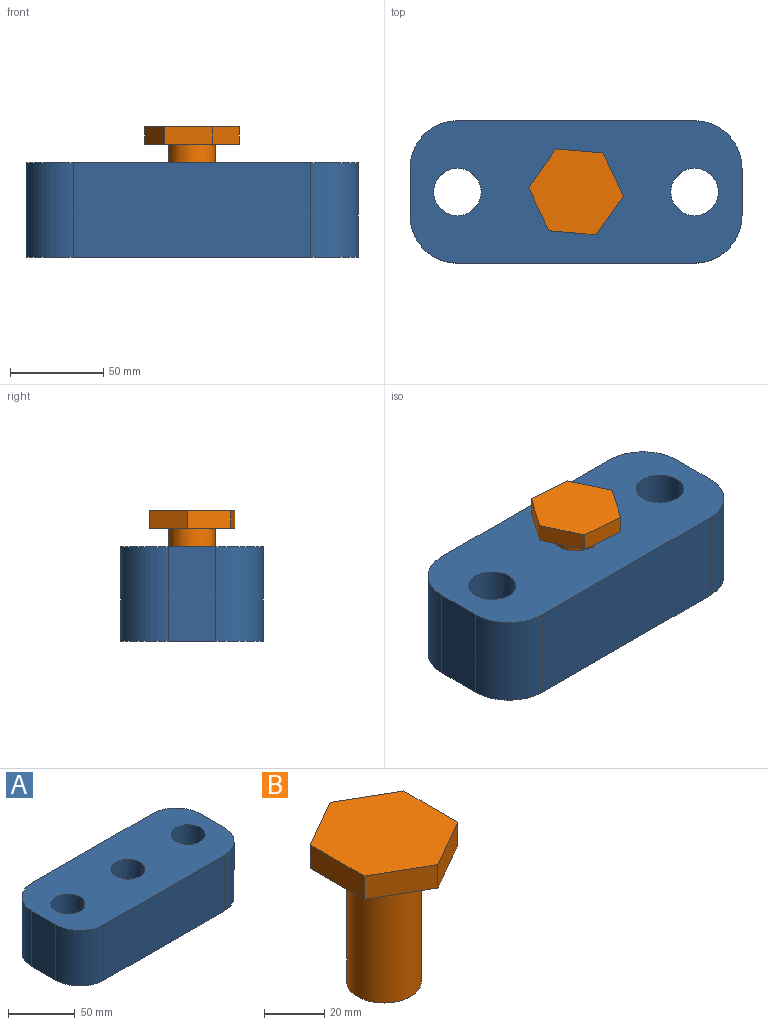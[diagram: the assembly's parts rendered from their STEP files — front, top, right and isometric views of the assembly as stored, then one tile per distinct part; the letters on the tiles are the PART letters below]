
ASSEMBLY  parts=2 mates=1
PART A: 13 faces, bbox 177.8x76.2x50.8 mm
  f0: plane 127x50.8mm, normal (0,1,0), area 6451.6mm2, adj f2,f3,f9,f12
  f1: plane 127x50.8mm, normal (0,-1,0), area 6451.6mm2, adj f2,f3,f10,f11
  f2: plane 177.8x76.2mm, normal (0,0,1), area 11474.4mm2, adj f0,f1,f4,f5,f6,f7,f8,f9
  f3: plane 177.8x76.2mm, normal (0,0,-1), area 11474.4mm2, adj f0,f1,f4,f5,f6,f7,f8,f9
  f4: cylinder r=12.7mm len=50.8mm, axis (0,0,1), area 4053.7mm2, adj f2,f3
  f5: plane 50.8x25.4mm, normal (-1,0,0), area 1290.3mm2, adj f2,f3,f9,f10
  f6: plane 50.8x25.4mm, normal (1,0,0), area 1290.3mm2, adj f2,f3,f11,f12
  f7: cylinder r=12.7mm len=50.8mm, axis (0,0,1), area 4053.7mm2, adj f2,f3
  f8: cylinder r=12.7mm len=50.8mm, axis (0,0,1), area 4053.7mm2, adj f2,f3
  f9: cylinder r=25.4mm len=50.8mm, axis (0,0,-1), area 2026.8mm2, adj f0,f2,f3,f5
  f10: cylinder r=25.4mm len=50.8mm, axis (0,0,1), area 2026.8mm2, adj f1,f2,f3,f5
  f11: cylinder r=25.4mm len=50.8mm, axis (0,0,1), area 2026.8mm2, adj f1,f2,f3,f6
  f12: cylinder r=25.4mm len=50.8mm, axis (0,0,-1), area 2026.8mm2, adj f0,f2,f3,f6
PART B: 10 faces, bbox 44x50.8x60.3 mm
  f0: cylinder r=12.45mm len=50.8mm, axis (0,0,1), area 3972.6mm2, adj f1,f9
  f1: plane 24.89x24.89mm, normal (0,0,-1), area 486.6mm2, adj f0
  f2: plane 25.4x9.53mm, normal (1,0,0), area 241.9mm2, adj f3,f7,f8,f9
  f3: plane 22x12.7mm, normal (0.5,0.87,0), area 241.9mm2, adj f2,f4,f8,f9
  f4: plane 22x12.7mm, normal (-0.5,0.87,0), area 241.9mm2, adj f3,f5,f8,f9
  f5: plane 25.4x9.53mm, normal (-1,0,0), area 241.9mm2, adj f4,f6,f8,f9
  f6: plane 22x12.7mm, normal (-0.5,-0.87,0), area 241.9mm2, adj f5,f7,f8,f9
  f7: plane 22x12.7mm, normal (0.5,-0.87,0), area 241.9mm2, adj f2,f6,f8,f9
  f8: plane 50.8x43.99mm, normal (0,0,1), area 1676.2mm2, adj f2,f3,f4,f5,f6,f7
  f9: plane 50.8x43.99mm, normal (0,0,-1), area 1189.5mm2, adj f0,f2,f3,f4,f5,f6,f7
PLACE A t=(-7.37,-0.66,-49.63)mm fixed
PLACE B rot(axis=(0,0,1),85deg) t=(-7.37,-0.66,-39.93)mm
MATE cylindrical A.f4 <-> B.f0  axis (0,0,1) through (-7.37,-0.66,-24.23)mm
